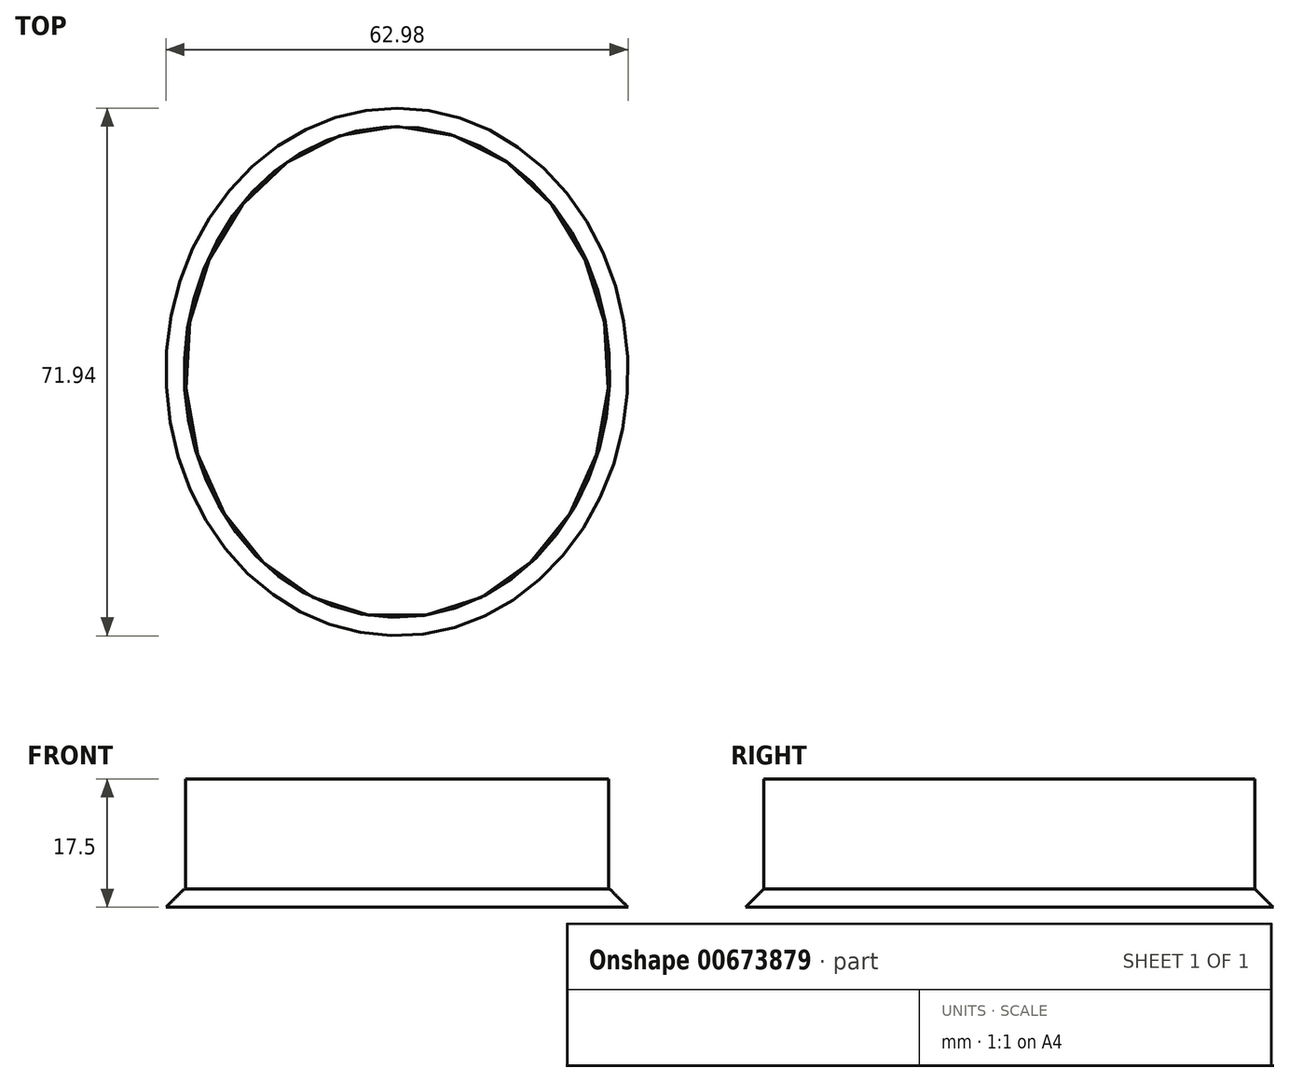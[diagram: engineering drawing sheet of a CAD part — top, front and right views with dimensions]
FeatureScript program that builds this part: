
annotation { "Feature Type Name" : "Feature", "Feature Type Description" : "" }
export const myFeature = defineFeature(function(context is Context, id is Id, definition is map)
    precondition{}
    {
        {
            var Q0;
            Q0=qCreatedBy(makeId("Top.planeOp"),FACE);
            var sketch = newSketch(context, id + "F0", { "sketchPlane" : qUnion([Q0])});
            skEllipse(sketch, "E0", {"center": v(0, 0) * mm, "majorRadius": 35.97 * mm, "minorRadius": 31.5 * mm, "majorAxis": v(0, 1)});
            skSolve(sketch);
        }
        {
            var Q0;
            Q0 = qSketchRegion(id + "F0", true);
            extrude(context, id + "F1", {"entities" : qUnion([Q0]), "depth" : 2.5 * mm, "offsetDistance" : 25 * mm});
        }
        {
            var Q0;
            Q0=makeQuery(id+"F1.opExtrude","CAP_FACE",FACE,{"disambiguationData":[OSD([sQuery(id+"F0.wireOp",EDGE,"E0")])],"isStart":false});
            var sketch = newSketch(context, id + "F2", { "sketchPlane" : qUnion([Q0])});
            skEllipse(sketch, "E1", {"center": v(0, 0) * mm, "majorRadius": 33.46 * mm, "minorRadius": 28.84 * mm, "majorAxis": v(0, 1)});
            skSolve(sketch);
        }
        {
            var Q0;
            Q0 = qSketchRegion(id + "F2", true);
            extrude(context, id + "F3", {"entities" : qUnion([Q0]), "operationType" : NewBodyOperationType.ADD, "depth" : 15 * mm, "offsetDistance" : 25 * mm});
        }
        {
            var Q0;
            Q0=makeQuery(id+"F1.opExtrude","CAP_EDGE",EDGE,{"disambiguationData":[OSD([sQuery(id+"F0.wireOp",EDGE,"E0")])],"isStart":false});
            chamfer(context, id + "F4", {"entities" : qUnion([Q0]), "width" : 2.5 * mm, "tangentPropagation" : true});
        }
    });
